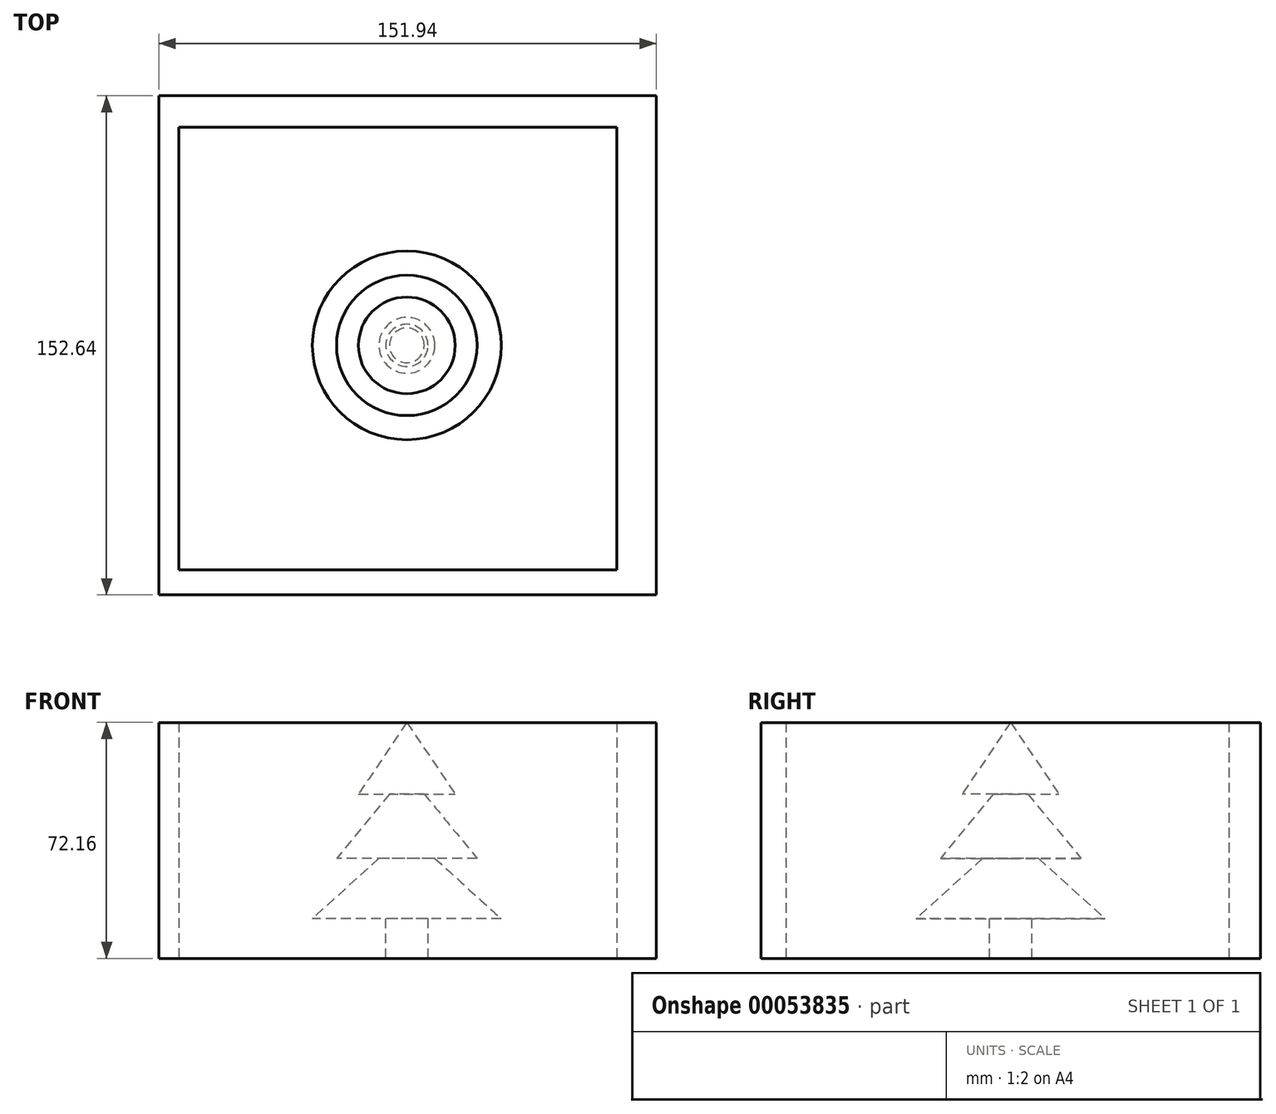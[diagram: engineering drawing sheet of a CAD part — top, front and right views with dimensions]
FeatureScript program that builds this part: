
annotation { "Feature Type Name" : "Feature", "Feature Type Description" : "" }
export const myFeature = defineFeature(function(context is Context, id is Id, definition is map)
    precondition{}
    {
        {
            var Q0;
            Q0=qCreatedBy(makeId("Front.planeOp"),FACE);
            var sketch = newSketch(context, id + "F0", { "sketchPlane" : qUnion([Q0])});
            skLineSegment(sketch, "E0", {"start": v(-11.55, 12.12) * mm, "end": v(-28.86, 12.12) * mm});
            skLineSegment(sketch, "E1", {"start": v(-28.86, 12.12) * mm, "end": v(-8.54, 30.6) * mm});
            skLineSegment(sketch, "E2", {"start": v(-8.54, 30.6) * mm, "end": v(-21.47, 30.6) * mm});
            skLineSegment(sketch, "E3", {"start": v(-21.47, 30.6) * mm, "end": v(-5.31, 50.22) * mm});
            skLineSegment(sketch, "E4", {"start": v(-5.31, 50.22) * mm, "end": v(-14.78, 50.22) * mm});
            skLineSegment(sketch, "E5", {"start": v(-14.78, 50.22) * mm, "end": v(0, 72.16) * mm});
            skLineSegment(sketch, "E6", {"start": v(-11.55, 12.12) * mm, "end": v(-6.47, 12.12) * mm});
            skLineSegment(sketch, "E7", {"start": v(-6.47, 12.12) * mm, "end": v(-6.47, 0) * mm});
            skLineSegment(sketch, "E8", {"start": v(0, 0) * mm, "end": v(-6.47, 0) * mm});
            skLineSegment(sketch, "E9", {"start": v(0, 72.16) * mm, "end": v(0, 0) * mm});
            skSolve(sketch);
        }
        {
            var Q0;
            Q0 = qSketchRegion(id + "F0", true);
            var Q1;
            Q1=sQuery(id+"F0.wireOp",EDGE,"E9");
            revolve(context, id + "F1", {"entities" : qUnion([Q0]), "axis" : qUnion([Q1]), "revolveType" : RevolveType.FULL});
        }
        {
            var Q0;
            Q0=qCreatedBy(makeId("Top.planeOp"),FACE);
            var sketch = newSketch(context, id + "F2", { "sketchPlane" : qUnion([Q0])});
            skLineSegment(sketch, "E10.bottom", {"start": v(-75.74, 76.32) * mm, "end": v(76.2, 76.32) * mm});
            skLineSegment(sketch, "E10.top", {"start": v(-75.74, -76.32) * mm, "end": v(76.2, -76.32) * mm});
            skLineSegment(sketch, "E10.left", {"start": v(-75.74, 76.32) * mm, "end": v(-75.74, -76.32) * mm});
            skLineSegment(sketch, "E10.right", {"start": v(76.2, 76.32) * mm, "end": v(76.2, -76.32) * mm});
            skSolve(sketch);
        }
        {
            var Q0;
            Q0=makeQuery(id+"F2.imprint","IMPRINT",FACE,{"disambiguationData":[TD([[makeQuery(id+"F2.imprint","IMPRINT",EDGE,{"derivedFrom":sQuery(id+"F2.wireOp",EDGE,"E10.bottom")}),-1.0]])]});
            var sketch = newSketch(context, id + "F3", { "sketchPlane" : qUnion([Q0])});
            skLineSegment(sketch, "E11.right", {"start": v(64.12, -68.62) * mm, "end": v(64.12, 66.67) * mm});
            skLineSegment(sketch, "E12.top", {"start": v(-69.73, 66.67) * mm, "end": v(64.12, 66.67) * mm});
            skLineSegment(sketch, "E13.top", {"start": v(-69.73, -68.62) * mm, "end": v(64.12, -68.62) * mm});
            skLineSegment(sketch, "E14.right", {"start": v(-69.73, -68.62) * mm, "end": v(-69.73, 66.67) * mm});
            skSolve(sketch);
        }
        {
            var Q0;
            Q0=makeQuery(id+"F3.imprint","IMPRINT",FACE,{"disambiguationData":[TD([[makeQuery(id+"F3.imprint","IMPRINT",EDGE,{"derivedFrom":sQuery(id+"F3.wireOp",EDGE,"E11.right")}),-1.0]])]});
            extrude(context, id + "F4", {"entities" : qUnion([Q0]), "depth" : 72.12 * mm});
        }
    });
